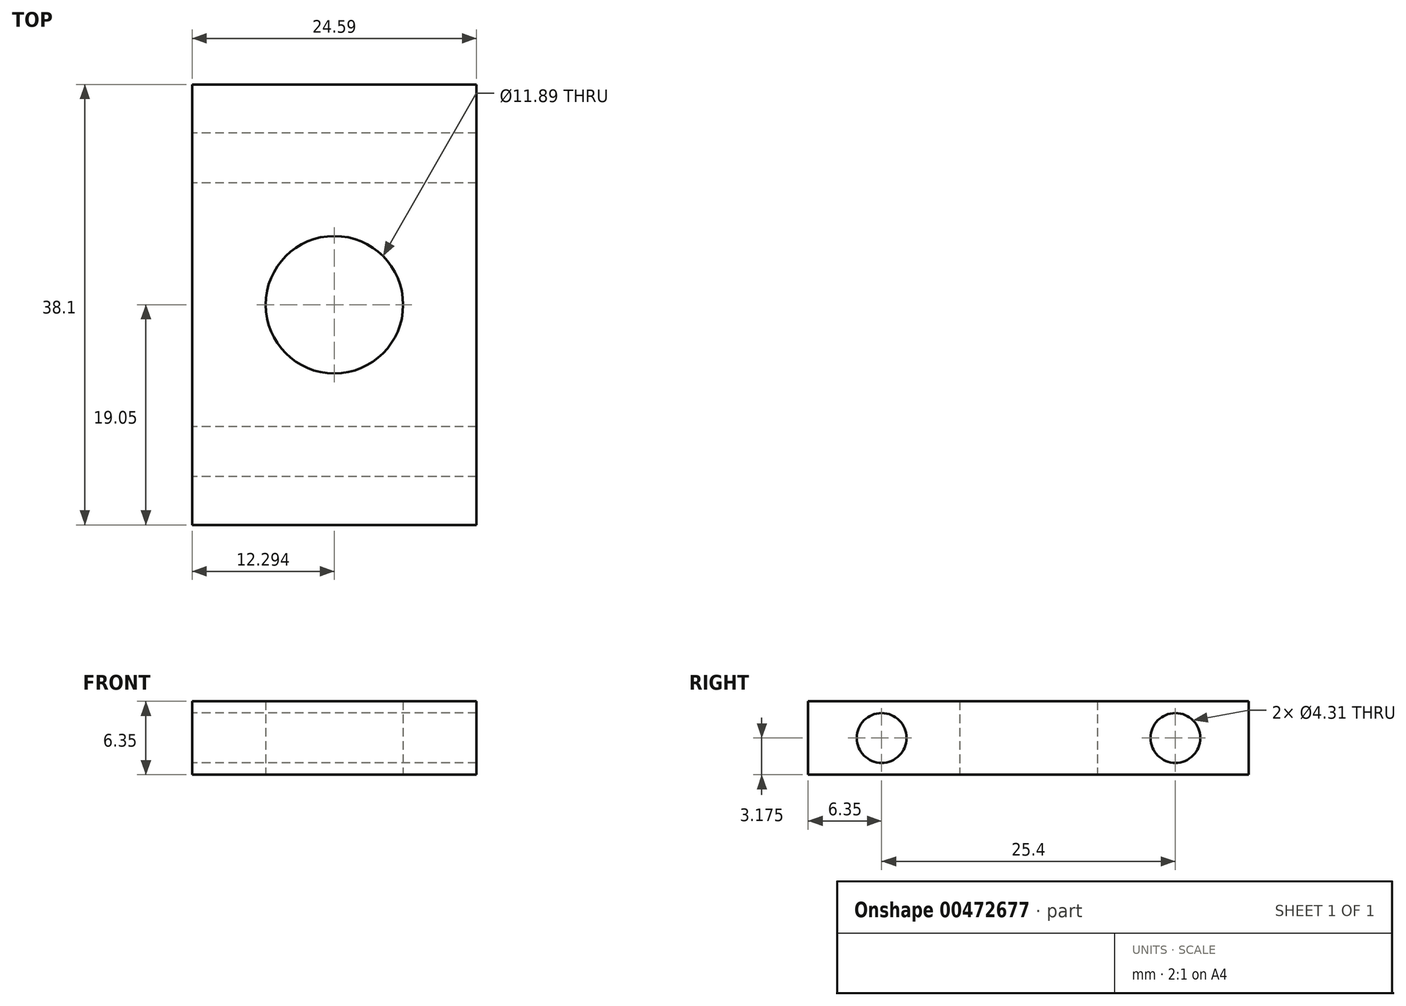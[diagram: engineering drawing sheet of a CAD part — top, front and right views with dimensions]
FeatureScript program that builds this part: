
annotation { "Feature Type Name" : "Feature", "Feature Type Description" : "" }
export const myFeature = defineFeature(function(context is Context, id is Id, definition is map)
    precondition{}
    {
        {
            var Q0;
            Q0=qCreatedBy(makeId("Top.planeOp"),FACE);
            var sketch = newSketch(context, id + "F0", { "sketchPlane" : qUnion([Q0])});
            skLineSegment(sketch, "E0.bottom", {"start": v(0, 0) * mm, "end": v(24.59, 0) * mm});
            skLineSegment(sketch, "E0.top", {"start": v(0, 38.1) * mm, "end": v(24.59, 38.1) * mm});
            skLineSegment(sketch, "E0.left", {"start": v(0, 0) * mm, "end": v(0, 38.1) * mm});
            skLineSegment(sketch, "E1", {"start": v(24.59, 38.1) * mm, "end": v(24.59, 0) * mm});
            skCircle(sketch, "E2", {"center": v(12.3, 19.05) * mm, "radius": 5.94 * mm});
            skLineSegment(sketch, "E3", {"start": v(12.3, 19.05) * mm, "end": v(0, 19.05) * mm, "construction": true});
            skSolve(sketch);
        }
        {
            var Q0;
            Q0 = qSketchRegion(id + "F0", true);
            extrude(context, id + "F1", {"entities" : qUnion([Q0]), "depth" : 6.35 * mm, "offsetDistance" : 25.4 * mm});
        }
        {
            var Q0;
            Q0=makeQuery(id+"F1.opExtrude","SWEPT_FACE",FACE,{"disambiguationData":[OSD([sQuery(id+"F0.wireOp",EDGE,"E0.left")])]});
            var sketch = newSketch(context, id + "F2", { "sketchPlane" : qUnion([Q0])});
            skCircle(sketch, "E4", {"center": v(-31.75, 3.17) * mm, "radius": 2.15 * mm});
            skLineSegment(sketch, "E5", {"start": v(-19.05, 6.35) * mm, "end": v(-19.05, 0) * mm, "construction": true});
            skCircle(sketch, "E6.MirrorC", {"center": v(-6.35, 3.18) * mm, "radius": 2.15 * mm});
            skLineSegment(sketch, "E7", {"start": v(-31.75, 3.17) * mm, "end": v(-38.1, 3.17) * mm, "construction": true});
            skSolve(sketch);
        }
        {
            var Q0;
            Q0 = qSketchRegion(id + "F2", true);
            extrude(context, id + "F3", {"entities" : qUnion([Q0]), "operationType" : NewBodyOperationType.REMOVE, "endBound" : BoundingType.THROUGH_ALL, "oppositeDirection" : true, "depth" : 12.7 * mm, "offsetDistance" : 25.4 * mm});
        }
    });
